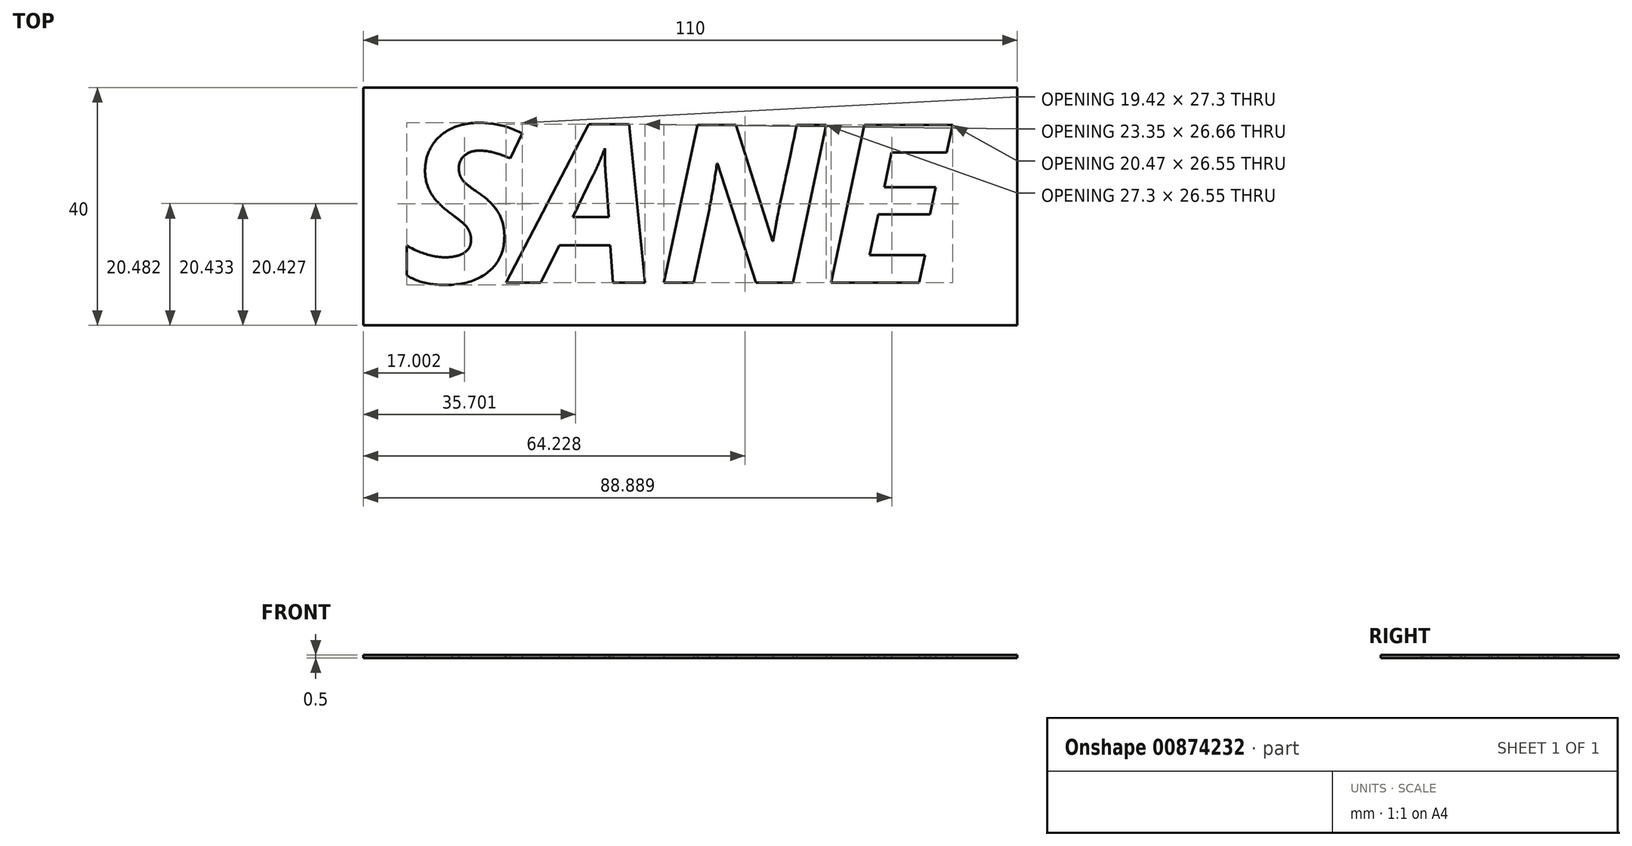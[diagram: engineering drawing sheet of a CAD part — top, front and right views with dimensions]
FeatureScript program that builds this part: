
annotation { "Feature Type Name" : "Feature", "Feature Type Description" : "" }
export const myFeature = defineFeature(function(context is Context, id is Id, definition is map)
    precondition{}
    {
        {
            var Q0;
            Q0=qCreatedBy(makeId("Top.planeOp"),FACE);
            var sketch = newSketch(context, id + "F0", { "sketchPlane" : qUnion([Q0])});
            skLineSegment(sketch, "E0.bottom", {"start": v(55, -20) * mm, "end": v(-55, -20) * mm});
            skLineSegment(sketch, "E0.top", {"start": v(55, 20) * mm, "end": v(-55, 20) * mm});
            skLineSegment(sketch, "E0.left", {"start": v(55, -20) * mm, "end": v(55, 20) * mm});
            skLineSegment(sketch, "E0.right", {"start": v(-55, -20) * mm, "end": v(-55, 20) * mm});
            skPoint(sketch, "E0.middle", {"position": v(0, 0) * mm});
            skLineSegment(sketch, "E1", {"start": v(0, 20) * mm, "end": v(0, -20) * mm, "construction": true});
            skLineSegment(sketch, "E2", {"start": v(55, 0) * mm, "end": v(-55, 0) * mm, "construction": true});
            skText(sketch, "E3", { "text": "SANE", "fontName": "OpenSans-BoldItalic.ttf"});
            const initialGuessF0  = {"E3": [-0.04845, -0.01285, 1, 0, 0.02678]};
            skSetInitialGuess(sketch, initialGuessF0);
            skSolve(sketch);
        }
        {
            var Q0;
            Q0=makeQuery(id+"F0.imprint","IMPRINT",FACE,{"disambiguationData":[TD([[makeQuery(id+"F0.imprint","IMPRINT",EDGE,{"derivedFrom":sQuery(id+"F0.wireOp",EDGE,"E0.bottom")}),-1.0]])]});
            var Q1;
            Q1=makeQuery(id+"F0.imprint","IMPRINT",FACE,{"disambiguationData":[TD([[makeQuery(id+"F0.imprint","IMPRINT",EDGE,{"derivedFrom":sQuery(id+"F0.wireOp",EDGE,"a4058165-274c-448f-8c76-c7f7474ecb35.sketch_text.stroke-11")}),1.0]])]});
            var Q2;
            Q2=makeQuery(id+"F0.imprint","IMPRINT",FACE,{"disambiguationData":[TD([[makeQuery(id+"F0.imprint","IMPRINT",EDGE,{"derivedFrom":sQuery(id+"F0.wireOp",EDGE,"a4058165-274c-448f-8c76-c7f7474ecb35.sketch_text.stroke-53")}),1.0]])]});
            var Q3;
            Q3=makeQuery(id+"F0.imprint","IMPRINT",FACE,{"disambiguationData":[TD([[makeQuery(id+"F0.imprint","IMPRINT",EDGE,{"derivedFrom":sQuery(id+"F0.wireOp",EDGE,"E3.sketch_text.stroke-32")}),1.0]])]});
            extrude(context, id + "F1", {"entities" : qUnion([Q0, Q1, Q2, Q3]), "depth" : 0.5 * mm, "offsetDistance" : 25 * mm});
        }
    });
